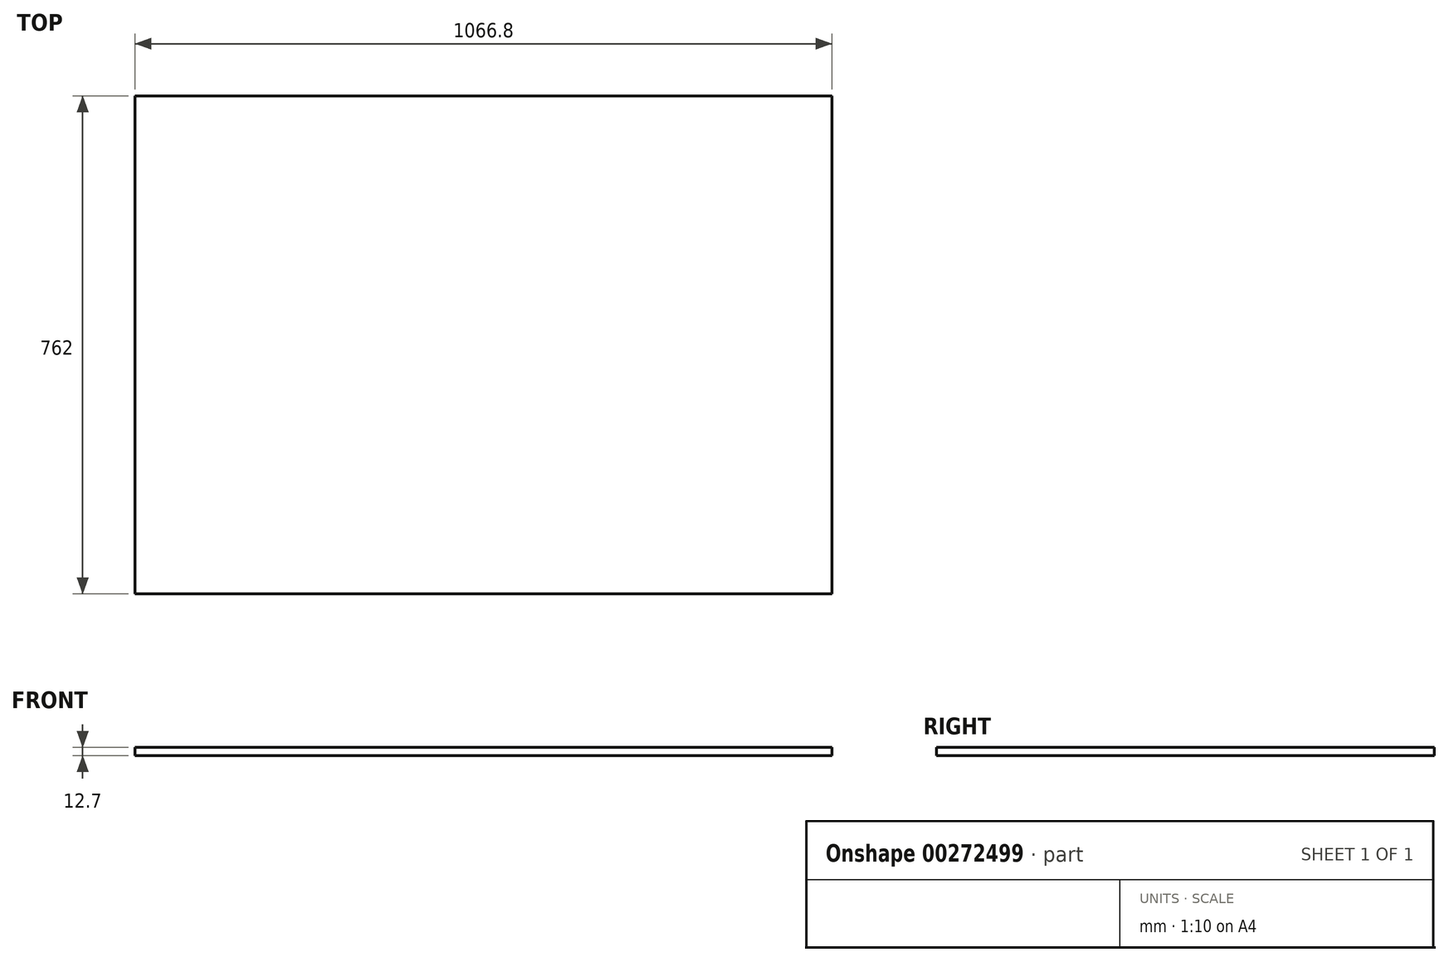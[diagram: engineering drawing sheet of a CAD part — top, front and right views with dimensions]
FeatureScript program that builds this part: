
annotation { "Feature Type Name" : "Feature", "Feature Type Description" : "" }
export const myFeature = defineFeature(function(context is Context, id is Id, definition is map)
    precondition{}
    {
        {
            var Q0;
            Q0=qCreatedBy(makeId("Top.planeOp"), FACE);
            var sketch = newSketch(context, id + "F0", { "sketchPlane" : qUnion([Q0])});
            skLineSegment(sketch, "E0.bottom", {"start": v(533.4, 381) * mm, "end": v(-533.4, 381) * mm});
            skLineSegment(sketch, "E0.top", {"start": v(533.4, -381) * mm, "end": v(-533.4, -381) * mm});
            skLineSegment(sketch, "E0.left", {"start": v(533.4, 381) * mm, "end": v(533.4, -381) * mm});
            skLineSegment(sketch, "E0.right", {"start": v(-533.4, 381) * mm, "end": v(-533.4, -381) * mm});
            skPoint(sketch, "E0.middle", {"position": v(0, 0) * mm});
            skSolve(sketch);
        }
        {
            var Q0;
            Q0 = qSketchRegion(id + "F0", true);
            extrude(context, id + "F1", {"entities" : qUnion([Q0]), "depth" : 12.7 * mm, "offsetDistance" : 25.4 * mm});
        }
    });
